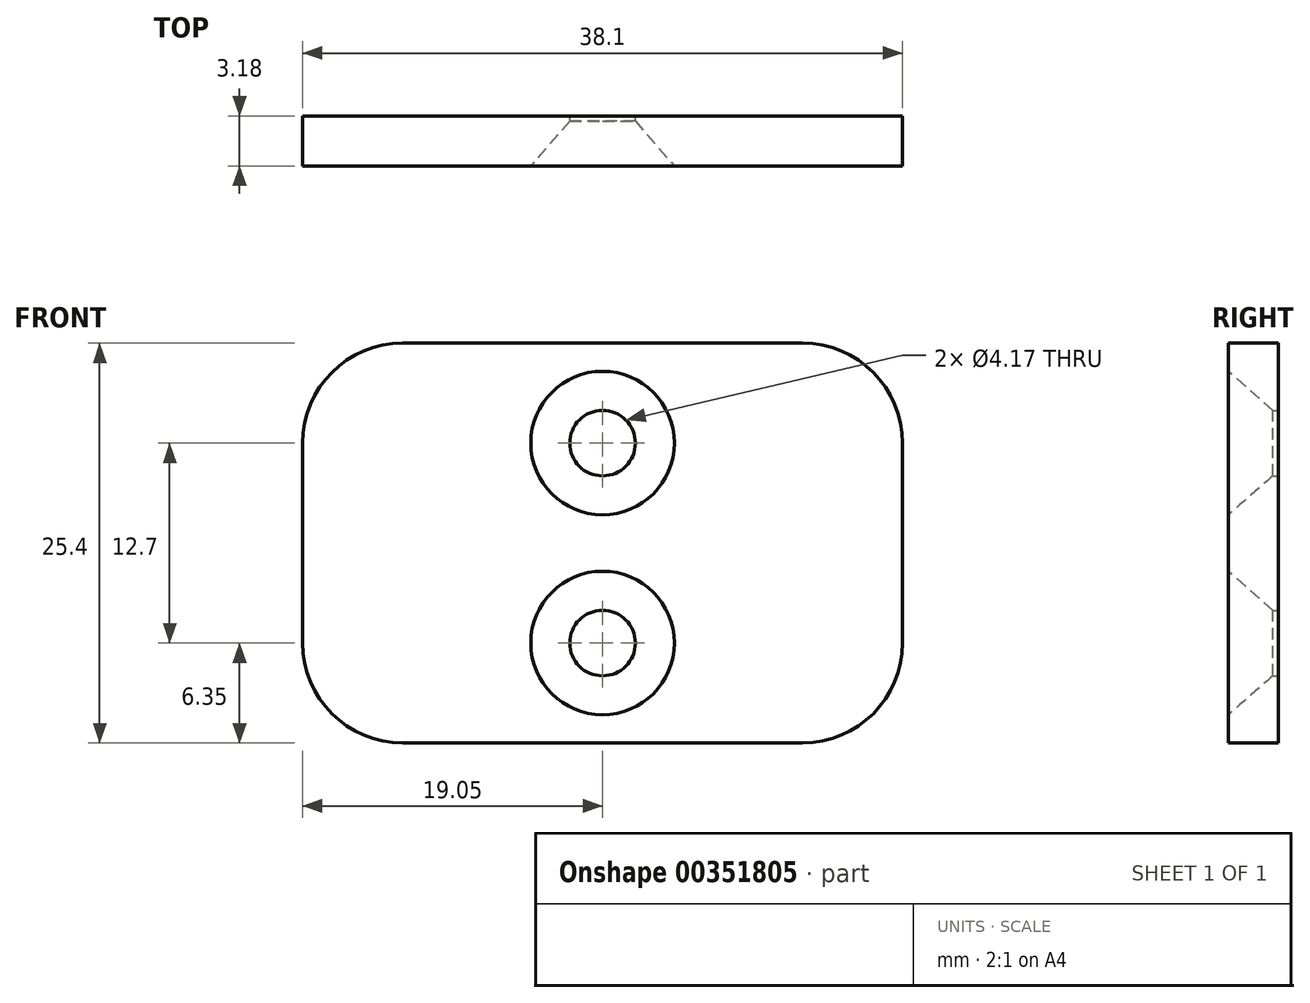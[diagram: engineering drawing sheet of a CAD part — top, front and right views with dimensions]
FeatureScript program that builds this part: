
annotation { "Feature Type Name" : "Feature", "Feature Type Description" : "" }
export const myFeature = defineFeature(function(context is Context, id is Id, definition is map)
    precondition{}
    {
        {
            var Q0;
            Q0=qCreatedBy(makeId("Front.planeOp"),FACE);
            var sketch = newSketch(context, id + "F0", { "sketchPlane" : qUnion([Q0])});
            skLineSegment(sketch, "E0.bottom", {"start": v(6.35, 0) * mm, "end": v(31.75, 0) * mm});
            skLineSegment(sketch, "E0.top", {"start": v(6.35, 25.4) * mm, "end": v(31.75, 25.4) * mm});
            skLineSegment(sketch, "E0.left", {"start": v(0, 6.35) * mm, "end": v(0, 19.05) * mm});
            skLineSegment(sketch, "E0.right", {"start": v(38.1, 6.35) * mm, "end": v(38.1, 19.05) * mm});
            skPoint(sketch, "E1.visualSharp", {"position": v(0, 25.4) * mm});
            skArc(sketch, "E1.filletArc", {"start": v(6.35, 25.4) * mm, "mid": v(1.86, 23.54) * mm, "end": v(0, 19.05) * mm});
            skPoint(sketch, "E2.visualSharp", {"position": v(0, 0) * mm});
            skArc(sketch, "E2.filletArc", {"start": v(0, 6.35) * mm, "mid": v(1.86, 1.86) * mm, "end": v(6.35, 0) * mm});
            skPoint(sketch, "E3.visualSharp", {"position": v(38.1, 0) * mm});
            skArc(sketch, "E3.filletArc", {"start": v(31.75, 0) * mm, "mid": v(36.24, 1.86) * mm, "end": v(38.1, 6.35) * mm});
            skPoint(sketch, "E4.visualSharp", {"position": v(38.1, 25.4) * mm});
            skArc(sketch, "E4.filletArc", {"start": v(38.1, 19.05) * mm, "mid": v(36.24, 23.54) * mm, "end": v(31.75, 25.4) * mm});
            skCircle(sketch, "E5", {"center": v(19.05, 19.05) * mm, "radius": 2.08 * mm});
            skCircle(sketch, "E6", {"center": v(19.05, 6.35) * mm, "radius": 2.08 * mm});
            skSolve(sketch);
        }
        {
            var Q0;
            Q0 = qSketchRegion(id + "F0", true);
            extrude(context, id + "F1", {"entities" : qUnion([Q0]), "depth" : 3.17 * mm});
        }
        {
            var Q0;
            Q0=makeQuery(id+"F1.opExtrude","CAP_EDGE",EDGE,{"disambiguationData":[OSD([sQuery(id+"F0.wireOp",EDGE,"E5")])],"isStart":false});
            var Q1;
            Q1=makeQuery(id+"F1.opExtrude","CAP_EDGE",EDGE,{"disambiguationData":[OSD([sQuery(id+"F0.wireOp",EDGE,"E6")])],"isStart":false});
            chamfer(context, id + "F2", {"entities" : qUnion([Q0, Q1]), "chamferType" : ChamferType.TWO_OFFSETS, "width1" : 2.84 * mm, "oppositeDirection" : false, "width2" : 2.48 * mm, "tangentPropagation" : true});
        }
    });
